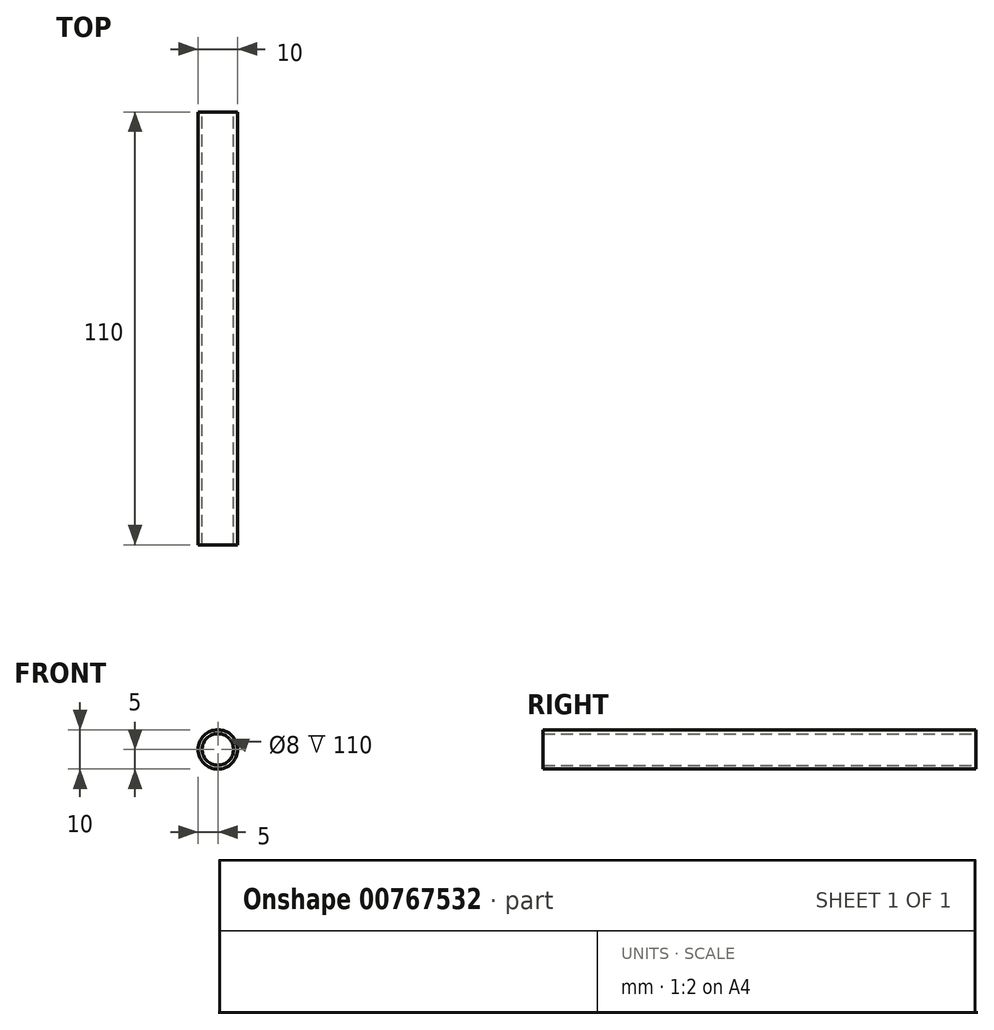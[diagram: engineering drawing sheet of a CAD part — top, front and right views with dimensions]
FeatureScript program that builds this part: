
annotation { "Feature Type Name" : "Feature", "Feature Type Description" : "" }
export const myFeature = defineFeature(function(context is Context, id is Id, definition is map)
    precondition{}
    {
        {
            var Q0;
            Q0=qCreatedBy(makeId("Front.planeOp"),FACE);
            var sketch = newSketch(context, id + "F0", { "sketchPlane" : qUnion([Q0])});
            skCircle(sketch, "E0", {"center": v(0, 0) * mm, "radius": 5 * mm});
            skCircle(sketch, "E1", {"center": v(0, 0) * mm, "radius": 4 * mm});
            skSolve(sketch);
        }
        {
            var Q0;
            Q0=makeQuery(id+"F0.imprint","IMPRINT",FACE,{"disambiguationData":[TD([[makeQuery(id+"F0.imprint","IMPRINT",EDGE,{"derivedFrom":sQuery(id+"F0.wireOp",EDGE,"E0")}),1.0]])]});
            extrude(context, id + "F1", {"entities" : qUnion([Q0]), "endBound" : BoundingType.SYMMETRIC, "depth" : 110 * mm, "offsetDistance" : 25 * mm});
        }
    });
